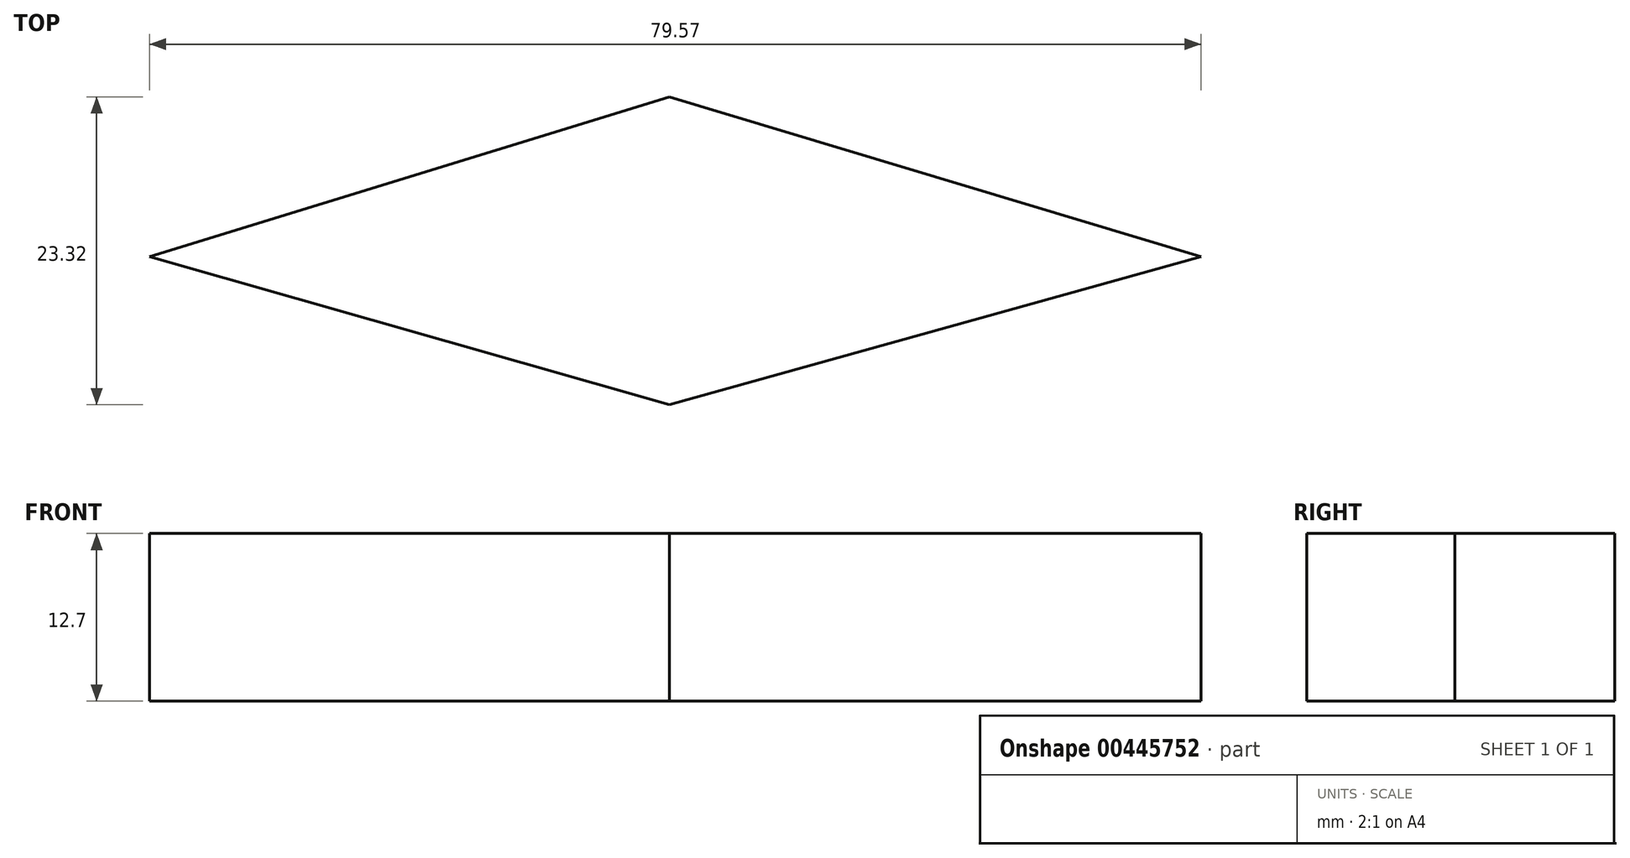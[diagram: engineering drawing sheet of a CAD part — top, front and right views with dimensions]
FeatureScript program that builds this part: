
annotation { "Feature Type Name" : "Feature", "Feature Type Description" : "" }
export const myFeature = defineFeature(function(context is Context, id is Id, definition is map)
    precondition{}
    {
        {
            var Q0;
            Q0=qCreatedBy(makeId("Top.planeOp"),FACE);
            var sketch = newSketch(context, id + "F0", { "sketchPlane" : qUnion([Q0])});
            skLineSegment(sketch, "E0", {"start": v(-39.35, 0) * mm, "end": v(0, 12.1) * mm});
            skLineSegment(sketch, "E1", {"start": v(0, 12.1) * mm, "end": v(40.22, 0) * mm});
            skLineSegment(sketch, "E2", {"start": v(40.22, 0) * mm, "end": v(0, -11.22) * mm});
            skLineSegment(sketch, "E3", {"start": v(0, -11.22) * mm, "end": v(-39.35, 0) * mm});
            skSolve(sketch);
        }
        {
            var Q0;
            Q0=makeQuery(id+"F0.imprint","IMPRINT",FACE,{"disambiguationData":[TD([[makeQuery(id+"F0.imprint","IMPRINT",EDGE,{"derivedFrom":sQuery(id+"F0.wireOp",EDGE,"E0")}),-1.0]])]});
            extrude(context, id + "F1", {"entities" : qUnion([Q0]), "depth" : 12.7 * mm});
        }
    });
